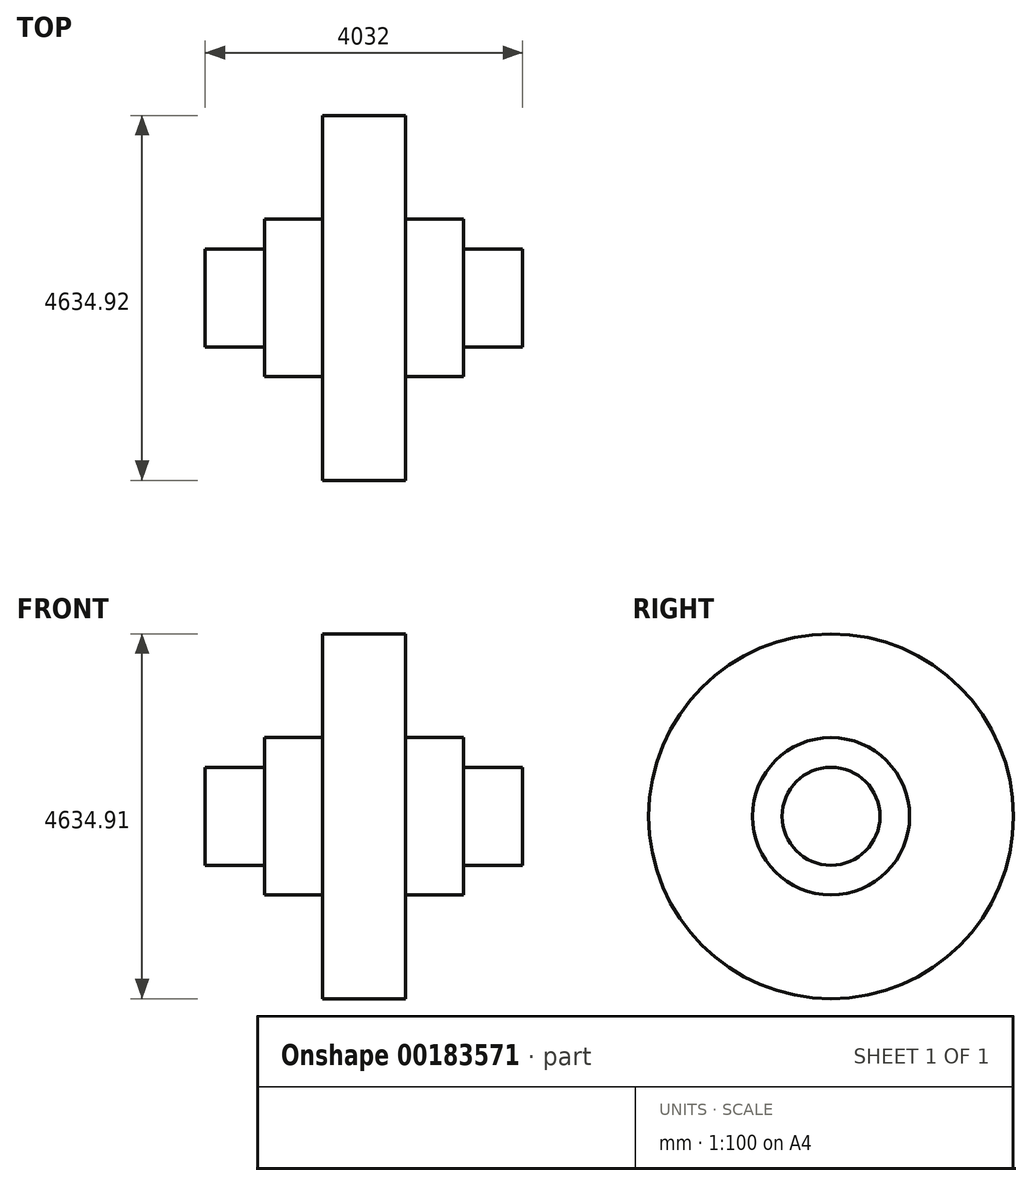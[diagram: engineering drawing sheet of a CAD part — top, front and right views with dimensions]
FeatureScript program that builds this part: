
annotation { "Feature Type Name" : "Feature", "Feature Type Description" : "" }
export const myFeature = defineFeature(function(context is Context, id is Id, definition is map)
    precondition{}
    {
        {
            var Q0;
            Q0=qCreatedBy(makeId("Front.planeOp"),FACE);
            var sketch = newSketch(context, id + "F0", { "sketchPlane" : qUnion([Q0])});
            skLineSegment(sketch, "E0", {"start": v(-830.59, 4356.65) * mm, "end": v(-303.04, 4356.65) * mm});
            skLineSegment(sketch, "E1", {"start": v(-303.04, 4356.65) * mm, "end": v(-303.04, 3037.77) * mm});
            skLineSegment(sketch, "E2", {"start": v(-303.04, 3037.77) * mm, "end": v(431.77, 3037.77) * mm});
            skLineSegment(sketch, "E3", {"start": v(431.77, 3037.77) * mm, "end": v(431.77, 2660.95) * mm});
            skLineSegment(sketch, "E4", {"start": v(1185.41, 2660.95) * mm, "end": v(1185.41, 2039.2) * mm});
            skLineSegment(sketch, "E5", {"start": v(431.77, 2660.95) * mm, "end": v(1185.41, 2660.95) * mm});
            skLineSegment(sketch, "E6", {"start": v(-830.59, 5317.55) * mm, "end": v(-830.59, -221.74) * mm, "construction": true});
            skLineSegment(sketch, "E7.MirrorCS", {"start": v(-2846.59, 2660.95) * mm, "end": v(-2846.59, 2039.2) * mm});
            skLineSegment(sketch, "E8.MirrorCS", {"start": v(-2092.94, 2660.95) * mm, "end": v(-2846.59, 2660.95) * mm});
            skLineSegment(sketch, "E9.MirrorCS", {"start": v(-2092.94, 3037.77) * mm, "end": v(-2092.94, 2660.95) * mm});
            skLineSegment(sketch, "E10.MirrorCS", {"start": v(-1358.14, 3037.77) * mm, "end": v(-2092.94, 3037.77) * mm});
            skLineSegment(sketch, "E11.MirrorCS", {"start": v(-830.59, 4356.65) * mm, "end": v(-1358.14, 4356.65) * mm});
            skLineSegment(sketch, "E12.MirrorCS", {"start": v(-1358.14, 4356.65) * mm, "end": v(-1358.14, 3037.77) * mm});
            skLineSegment(sketch, "E13", {"start": v(1185.41, 2039.2) * mm, "end": v(-2846.59, 2039.2) * mm});
            skSolve(sketch);
        }
        {
            var Q0;
            Q0 = qSketchRegion(id + "F0", true);
            var Q1;
            Q1=sQuery(id+"F0.wireOp",EDGE,"E13");
            revolve(context, id + "F1", {"entities" : qUnion([Q0]), "axis" : qUnion([Q1]), "revolveType" : RevolveType.FULL});
        }
    });
